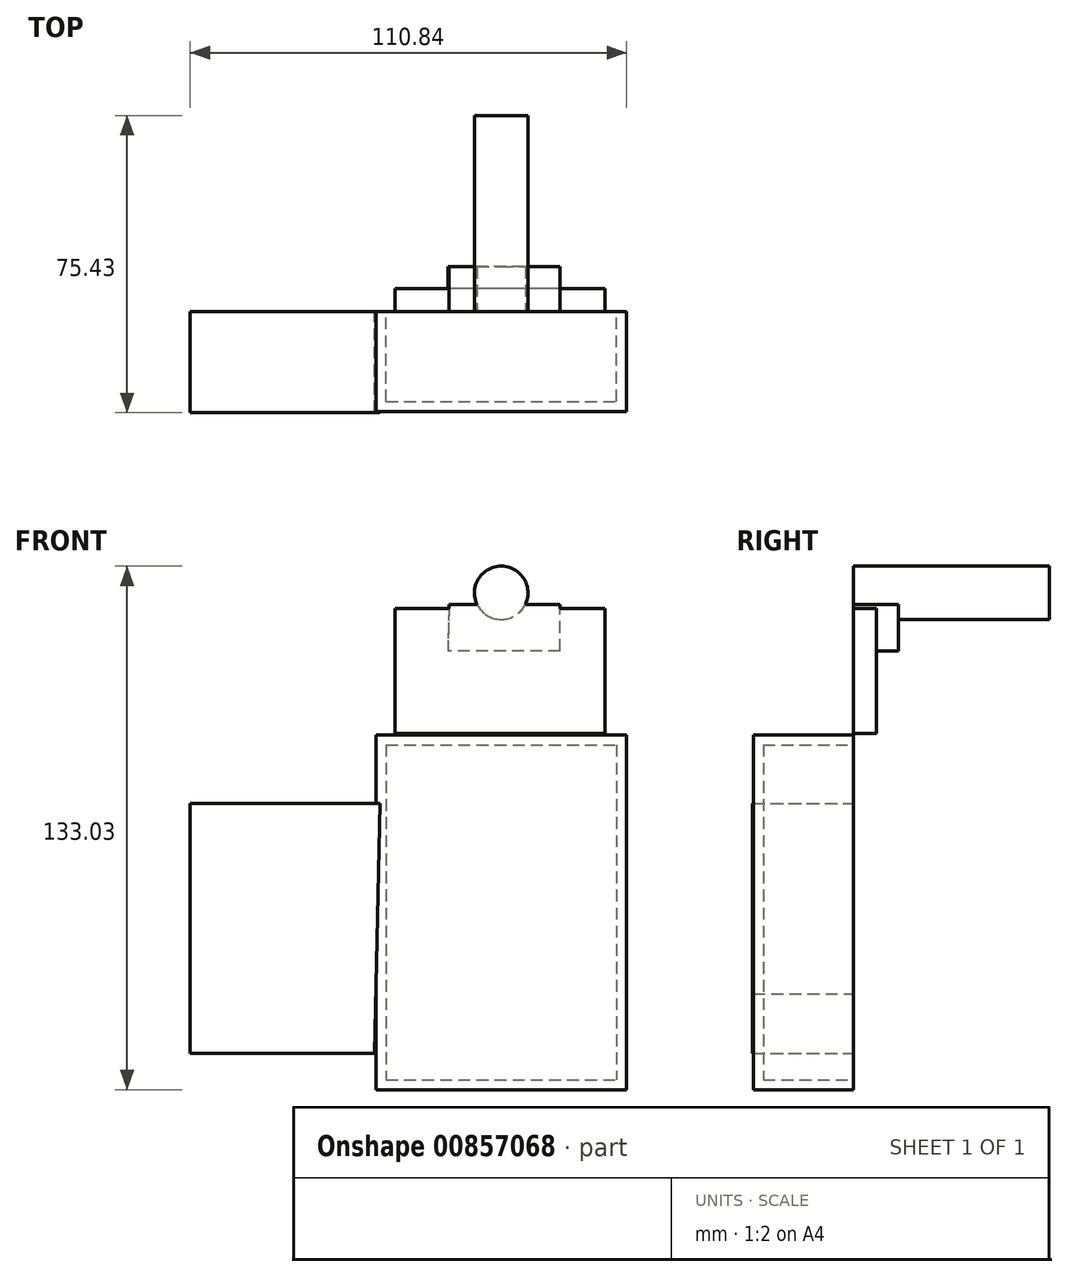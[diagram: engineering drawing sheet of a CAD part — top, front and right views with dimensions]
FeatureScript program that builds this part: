
annotation { "Feature Type Name" : "Feature", "Feature Type Description" : "" }
export const myFeature = defineFeature(function(context is Context, id is Id, definition is map)
    precondition{}
    {
        {
            var Q0;
            Q0=qCreatedBy(makeId("Front.planeOp"),FACE);
            var sketch = newSketch(context, id + "F0", { "sketchPlane" : qUnion([Q0])});
            skLineSegment(sketch, "E0.bottom", {"start": v(-31.8, 40.5) * mm, "end": v(31.8, 40.5) * mm});
            skLineSegment(sketch, "E0.top", {"start": v(-31.8, -49.68) * mm, "end": v(31.8, -49.68) * mm});
            skLineSegment(sketch, "E0.left", {"start": v(-31.8, 40.5) * mm, "end": v(-31.8, -49.68) * mm});
            skLineSegment(sketch, "E0.right", {"start": v(31.8, 40.5) * mm, "end": v(31.8, -49.68) * mm});
            skSolve(sketch);
        }
        {
            var Q0;
            Q0 = qSketchRegion(id + "F0", true);
            extrude(context, id + "F1", {"entities" : qUnion([Q0]), "depth" : 25.4 * mm, "offsetDistance" : 25.4 * mm});
        }
        {
            var Q0;
            Q0=makeQuery(id+"F1.opExtrude","CAP_FACE",FACE,{"disambiguationData":[OSD([sQuery(id+"F0.wireOp",EDGE,"E0.bottom"),sQuery(id+"F0.wireOp",EDGE,"E0.top"),sQuery(id+"F0.wireOp",EDGE,"E0.left"),sQuery(id+"F0.wireOp",EDGE,"E0.right")])],"isStart":true});
            shell(context, id + "F2", {"entities" : qUnion([Q0]), "thickness" : 2.54 * mm});
        }
        {
            var Q0;
            Q0=qCreatedBy(makeId("Front.planeOp"),FACE);
            var sketch = newSketch(context, id + "F3", { "sketchPlane" : qUnion([Q0])});
            skLineSegment(sketch, "E1", {"start": v(-30.77, 23) * mm, "end": v(-79.03, 23) * mm});
            skLineSegment(sketch, "E2", {"start": v(-79.03, 23) * mm, "end": v(-79.03, -40.5) * mm});
            skLineSegment(sketch, "E3", {"start": v(-79.03, -40.5) * mm, "end": v(-32.14, -40.5) * mm});
            skLineSegment(sketch, "E4", {"start": v(-30.77, 23) * mm, "end": v(-32.14, -40.5) * mm});
            skSolve(sketch);
        }
        {
            var Q0;
            Q0=makeQuery(id+"F3.imprint","IMPRINT",FACE,{"disambiguationData":[TD([[makeQuery(id+"F3.imprint","IMPRINT",EDGE,{"derivedFrom":sQuery(id+"F3.wireOp",EDGE,"E1")}),1.0]])]});
            extrude(context, id + "F4", {"entities" : qUnion([Q0]), "operationType" : NewBodyOperationType.ADD, "depth" : 25.65 * mm, "offsetDistance" : 25.4 * mm});
        }
        {
            var Q0;
            Q0=qCreatedBy(makeId("Front.planeOp"),FACE);
            var sketch = newSketch(context, id + "F5", { "sketchPlane" : qUnion([Q0])});
            skLineSegment(sketch, "E5.bottom", {"start": v(26.35, 40.82) * mm, "end": v(-27, 40.82) * mm});
            skLineSegment(sketch, "E5.top", {"start": v(26.35, 72.57) * mm, "end": v(-27, 72.57) * mm});
            skLineSegment(sketch, "E5.left", {"start": v(26.35, 40.82) * mm, "end": v(26.35, 72.57) * mm});
            skLineSegment(sketch, "E5.right", {"start": v(-27, 40.82) * mm, "end": v(-27, 72.57) * mm});
            skSolve(sketch);
        }
        {
            var Q0;
            Q0=makeQuery(id+"F5.imprint","IMPRINT",FACE,{"disambiguationData":[TD([[makeQuery(id+"F5.imprint","IMPRINT",EDGE,{"derivedFrom":sQuery(id+"F5.wireOp",EDGE,"E5.bottom")}),-1.0]])]});
            extrude(context, id + "F6", {"entities" : qUnion([Q0]), "oppositeDirection" : true, "depth" : 5.84 * mm, "offsetDistance" : 25.4 * mm});
        }
        {
            var Q0;
            Q0=qCreatedBy(makeId("Front.planeOp"),FACE);
            var sketch = newSketch(context, id + "F7", { "sketchPlane" : qUnion([Q0])});
            skLineSegment(sketch, "E6.bottom", {"start": v(14.98, 61.81) * mm, "end": v(-13.55, 61.81) * mm});
            skLineSegment(sketch, "E6.top", {"start": v(14.98, 61.48) * mm, "end": v(-13.55, 61.48) * mm});
            skLineSegment(sketch, "E6.left", {"start": v(14.98, 61.81) * mm, "end": v(14.98, 61.48) * mm});
            skLineSegment(sketch, "E6.right", {"start": v(-13.55, 61.81) * mm, "end": v(-13.55, 61.48) * mm});
            skLineSegment(sketch, "E7", {"start": v(14.98, 61.81) * mm, "end": v(14.98, 73.62) * mm});
            skLineSegment(sketch, "E8", {"start": v(14.98, 73.62) * mm, "end": v(-13.22, 73.62) * mm});
            skLineSegment(sketch, "E9", {"start": v(-13.22, 73.62) * mm, "end": v(-13.55, 61.81) * mm});
            skSolve(sketch);
        }
        {
            var Q0;
            Q0=makeQuery(id+"F7.imprint","IMPRINT",FACE,{"disambiguationData":[TD([[makeQuery(id+"F7.imprint","IMPRINT",EDGE,{"derivedFrom":sQuery(id+"F7.wireOp",EDGE,"E6.bottom")}),-1.0]])]});
            extrude(context, id + "F8", {"entities" : qUnion([Q0]), "operationType" : NewBodyOperationType.ADD, "oppositeDirection" : true, "depth" : 11.43 * mm, "offsetDistance" : 25.4 * mm});
        }
        {
            var Q0;
            Q0=qCreatedBy(makeId("Front.planeOp"),FACE);
            var sketch = newSketch(context, id + "F9", { "sketchPlane" : qUnion([Q0])});
            skCircle(sketch, "E10", {"center": v(0, 76.57) * mm, "radius": 6.79 * mm});
            skSolve(sketch);
        }
        {
            var Q0;
            Q0=makeQuery(id+"F9.imprint","IMPRINT",FACE,{"disambiguationData":[TD([[makeQuery(id+"F9.imprint","IMPRINT",EDGE,{"derivedFrom":sQuery(id+"F9.wireOp",EDGE,"E10")}),1.0]])]});
            extrude(context, id + "F10", {"entities" : qUnion([Q0]), "operationType" : NewBodyOperationType.ADD, "oppositeDirection" : true, "depth" : 49.78 * mm, "offsetDistance" : 25.4 * mm});
        }
    });
